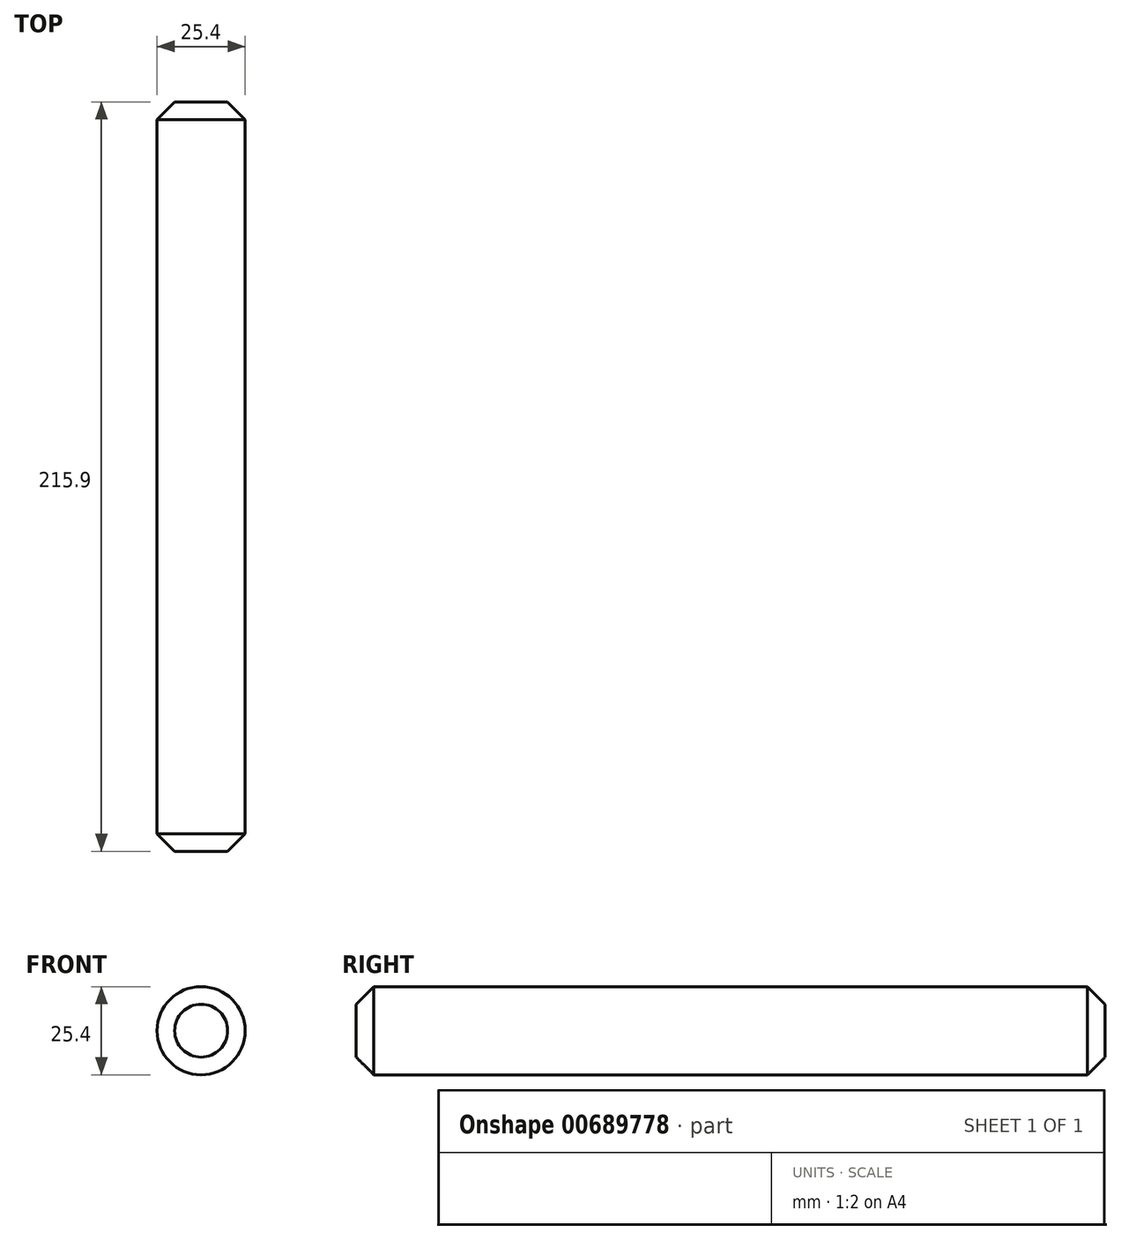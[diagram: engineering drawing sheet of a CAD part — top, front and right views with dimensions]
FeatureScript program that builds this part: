
annotation { "Feature Type Name" : "Feature", "Feature Type Description" : "" }
export const myFeature = defineFeature(function(context is Context, id is Id, definition is map)
    precondition{}
    {
        {
            var Q0;
            Q0=qCreatedBy(makeId("Front.planeOp"),FACE);
            var sketch = newSketch(context, id + "F0", { "sketchPlane" : qUnion([Q0])});
            skCircle(sketch, "E0", {"center": v(0, 0) * mm, "radius": 12.7 * mm});
            skSolve(sketch);
        }
        {
            var Q0;
            Q0=makeQuery(id+"F0.imprint","IMPRINT",FACE,{"disambiguationData":[TD([[makeQuery(id+"F0.imprint","IMPRINT",EDGE,{"derivedFrom":sQuery(id+"F0.wireOp",EDGE,"E0")}),1.0]])]});
            extrude(context, id + "F1", {"entities" : qUnion([Q0]), "oppositeDirection" : true, "depth" : 215.9 * mm, "offsetDistance" : 25.4 * mm});
        }
        {
            var Q0;
            Q0=makeQuery(id+"F1.opExtrude","CAP_EDGE",EDGE,{"disambiguationData":[OSD([sQuery(id+"F0.wireOp",EDGE,"E0")])],"isStart":true});
            var Q1;
            Q1=makeQuery(id+"F1.opExtrude","CAP_EDGE",EDGE,{"disambiguationData":[OSD([sQuery(id+"F0.wireOp",EDGE,"E0")])],"isStart":false});
            chamfer(context, id + "F2", {"entities" : qUnion([Q0, Q1]), "width" : 5.08 * mm, "tangentPropagation" : true});
        }
    });
